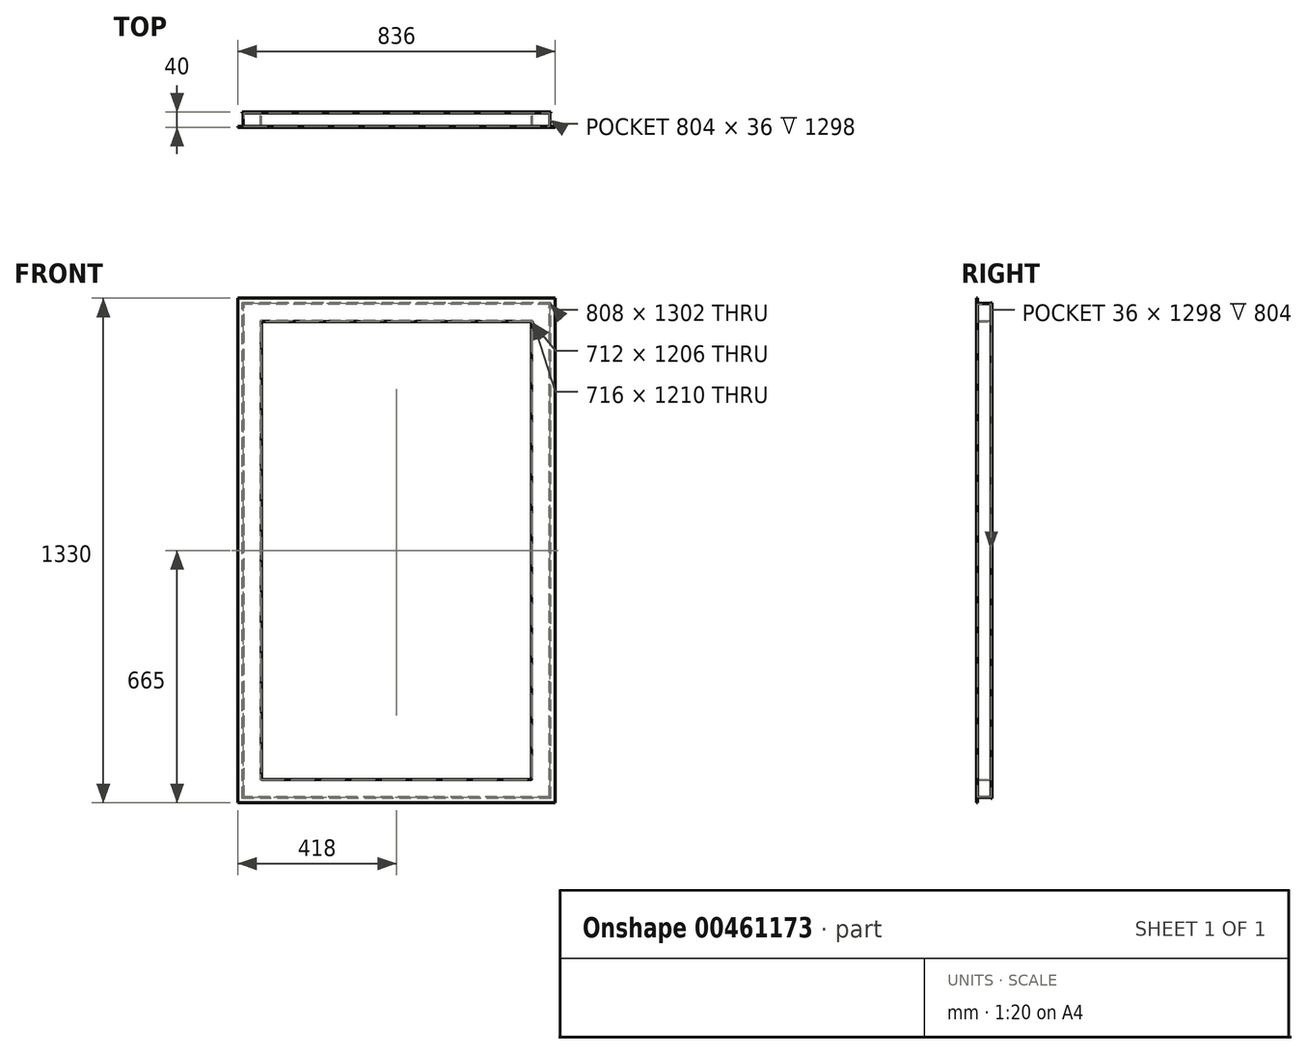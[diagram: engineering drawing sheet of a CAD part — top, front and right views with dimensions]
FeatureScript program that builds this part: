
annotation { "Feature Type Name" : "Feature", "Feature Type Description" : "" }
export const myFeature = defineFeature(function(context is Context, id is Id, definition is map)
    precondition{}
    {
        {
            var Q0;
            Q0=qCreatedBy(makeId("Front.planeOp"),FACE);
            var sketch = newSketch(context, id + "F0", { "sketchPlane" : qUnion([Q0])});
            skLineSegment(sketch, "E0.bottom", {"start": v(406, -653) * mm, "end": v(-406, -653) * mm});
            skLineSegment(sketch, "E0.top", {"start": v(406, 653) * mm, "end": v(-406, 653) * mm});
            skLineSegment(sketch, "E0.left", {"start": v(406, -653) * mm, "end": v(406, 653) * mm});
            skLineSegment(sketch, "E0.right", {"start": v(-406, -653) * mm, "end": v(-406, 653) * mm});
            skPoint(sketch, "E0.middle", {"position": v(0, 0) * mm});
            skLineSegment(sketch, "E1.0", {"start": v(356, -603) * mm, "end": v(356, 603) * mm});
            skLineSegment(sketch, "E2.0", {"start": v(356, -603) * mm, "end": v(-356, -603) * mm});
            skLineSegment(sketch, "E3.0", {"start": v(-356, -603) * mm, "end": v(-356, 603) * mm});
            skLineSegment(sketch, "E4.0", {"start": v(356, 603) * mm, "end": v(-356, 603) * mm});
            skSolve(sketch);
        }
        {
            var Q0;
            Q0 = qSketchRegion(id + "F0", true);
            extrude(context, id + "F1", {"entities" : qUnion([Q0]), "endBound" : BoundingType.SYMMETRIC, "depth" : 2 * mm});
        }
        {
            var Q0;
            Q0=makeQuery(id+"F1.opExtrude","CAP_FACE",FACE,{"disambiguationData":[OSD([sQuery(id+"F0.wireOp",EDGE,"E0.bottom"),sQuery(id+"F0.wireOp",EDGE,"E0.top"),sQuery(id+"F0.wireOp",EDGE,"E0.left"),sQuery(id+"F0.wireOp",EDGE,"E0.right"),sQuery(id+"F0.wireOp",EDGE,"E1.0"),sQuery(id+"F0.wireOp",EDGE,"E2.0"),sQuery(id+"F0.wireOp",EDGE,"E3.0"),sQuery(id+"F0.wireOp",EDGE,"E4.0")])],"isStart":false});
            var sketch = newSketch(context, id + "F2", { "sketchPlane" : qUnion([Q0])});
            skLineSegment(sketch, "E5.bottom", {"start": v(404, -651) * mm, "end": v(-404, -651) * mm});
            skLineSegment(sketch, "E5.top", {"start": v(404, 651) * mm, "end": v(-404, 651) * mm});
            skLineSegment(sketch, "E5.left", {"start": v(404, -651) * mm, "end": v(404, 651) * mm});
            skLineSegment(sketch, "E5.right", {"start": v(-404, -651) * mm, "end": v(-404, 651) * mm});
            skPoint(sketch, "E5.middle", {"position": v(0, 0) * mm});
            skLineSegment(sketch, "E6.0", {"start": v(402, -649) * mm, "end": v(402, 649) * mm});
            skLineSegment(sketch, "E7.0", {"start": v(402, 649) * mm, "end": v(-402, 649) * mm});
            skLineSegment(sketch, "E8.0", {"start": v(-402, -649) * mm, "end": v(-402, 649) * mm});
            skLineSegment(sketch, "E9.0", {"start": v(402, -649) * mm, "end": v(-402, -649) * mm});
            skLineSegment(sketch, "E10.0", {"start": v(-356, -603) * mm, "end": v(-356, 603) * mm});
            skLineSegment(sketch, "E11.0", {"start": v(356, 603) * mm, "end": v(-356, 603) * mm});
            skLineSegment(sketch, "E12.0", {"start": v(356, -603) * mm, "end": v(356, 603) * mm});
            skLineSegment(sketch, "E13.0", {"start": v(356, -603) * mm, "end": v(-356, -603) * mm});
            skLineSegment(sketch, "E14.0", {"start": v(358, -605) * mm, "end": v(-358, -605) * mm});
            skLineSegment(sketch, "E15.0", {"start": v(-358, -605) * mm, "end": v(-358, 605) * mm});
            skLineSegment(sketch, "E16.0", {"start": v(358, 605) * mm, "end": v(-358, 605) * mm});
            skLineSegment(sketch, "E17.0", {"start": v(358, -605) * mm, "end": v(358, 605) * mm});
            skSolve(sketch);
        }
        {
            var Q0;
            Q0=makeQuery(id+"F2.imprint","IMPRINT",FACE,{"disambiguationData":[TD([[makeQuery(id+"F2.imprint","IMPRINT",EDGE,{"derivedFrom":sQuery(id+"F2.wireOp",EDGE,"E5.bottom")}),-1.0]])]});
            var Q1;
            Q1=makeQuery(id+"F2.imprint","IMPRINT",FACE,{"disambiguationData":[TD([[makeQuery(id+"F2.imprint","IMPRINT",EDGE,{"derivedFrom":sQuery(id+"F2.wireOp",EDGE,"E10.0")}),1.0]])]});
            extrude(context, id + "F3", {"entities" : qUnion([Q0, Q1]), "operationType" : NewBodyOperationType.ADD, "depth" : 36 * mm});
        }
        {
            var Q0;
            Q0=makeQuery(id+"F3.opExtrude","CAP_FACE",FACE,{"disambiguationData":[OSD([sQuery(id+"F2.wireOp",EDGE,"E5.bottom"),sQuery(id+"F2.wireOp",EDGE,"E5.top"),sQuery(id+"F2.wireOp",EDGE,"E5.left"),sQuery(id+"F2.wireOp",EDGE,"E5.right"),sQuery(id+"F2.wireOp",EDGE,"E6.0"),sQuery(id+"F2.wireOp",EDGE,"E7.0"),sQuery(id+"F2.wireOp",EDGE,"E8.0"),sQuery(id+"F2.wireOp",EDGE,"E9.0")])],"isStart":false});
            var sketch = newSketch(context, id + "F4", { "sketchPlane" : qUnion([Q0])});
            skLineSegment(sketch, "E18.bottom", {"start": v(418, -665) * mm, "end": v(-418, -665) * mm});
            skLineSegment(sketch, "E18.top", {"start": v(418, 665) * mm, "end": v(-418, 665) * mm});
            skLineSegment(sketch, "E18.left", {"start": v(418, -665) * mm, "end": v(418, 665) * mm});
            skLineSegment(sketch, "E18.right", {"start": v(-418, -665) * mm, "end": v(-418, 665) * mm});
            skPoint(sketch, "E18.middle", {"position": v(0, 0) * mm});
            skLineSegment(sketch, "E19.0", {"start": v(358, 605) * mm, "end": v(-358, 605) * mm});
            skLineSegment(sketch, "E20.0", {"start": v(-356, -603) * mm, "end": v(-356, 603) * mm});
            skLineSegment(sketch, "E21.0", {"start": v(356, -603) * mm, "end": v(356, 603) * mm});
            skLineSegment(sketch, "E22.0", {"start": v(356, -603) * mm, "end": v(-356, -603) * mm});
            skLineSegment(sketch, "E23.0", {"start": v(356, 603) * mm, "end": v(-356, 603) * mm});
            skSolve(sketch);
        }
        {
            var Q0;
            Q0 = qSketchRegion(id + "F4", true);
            extrude(context, id + "F5", {"entities" : qUnion([Q0]), "operationType" : NewBodyOperationType.ADD, "depth" : 2 * mm});
        }
    });
